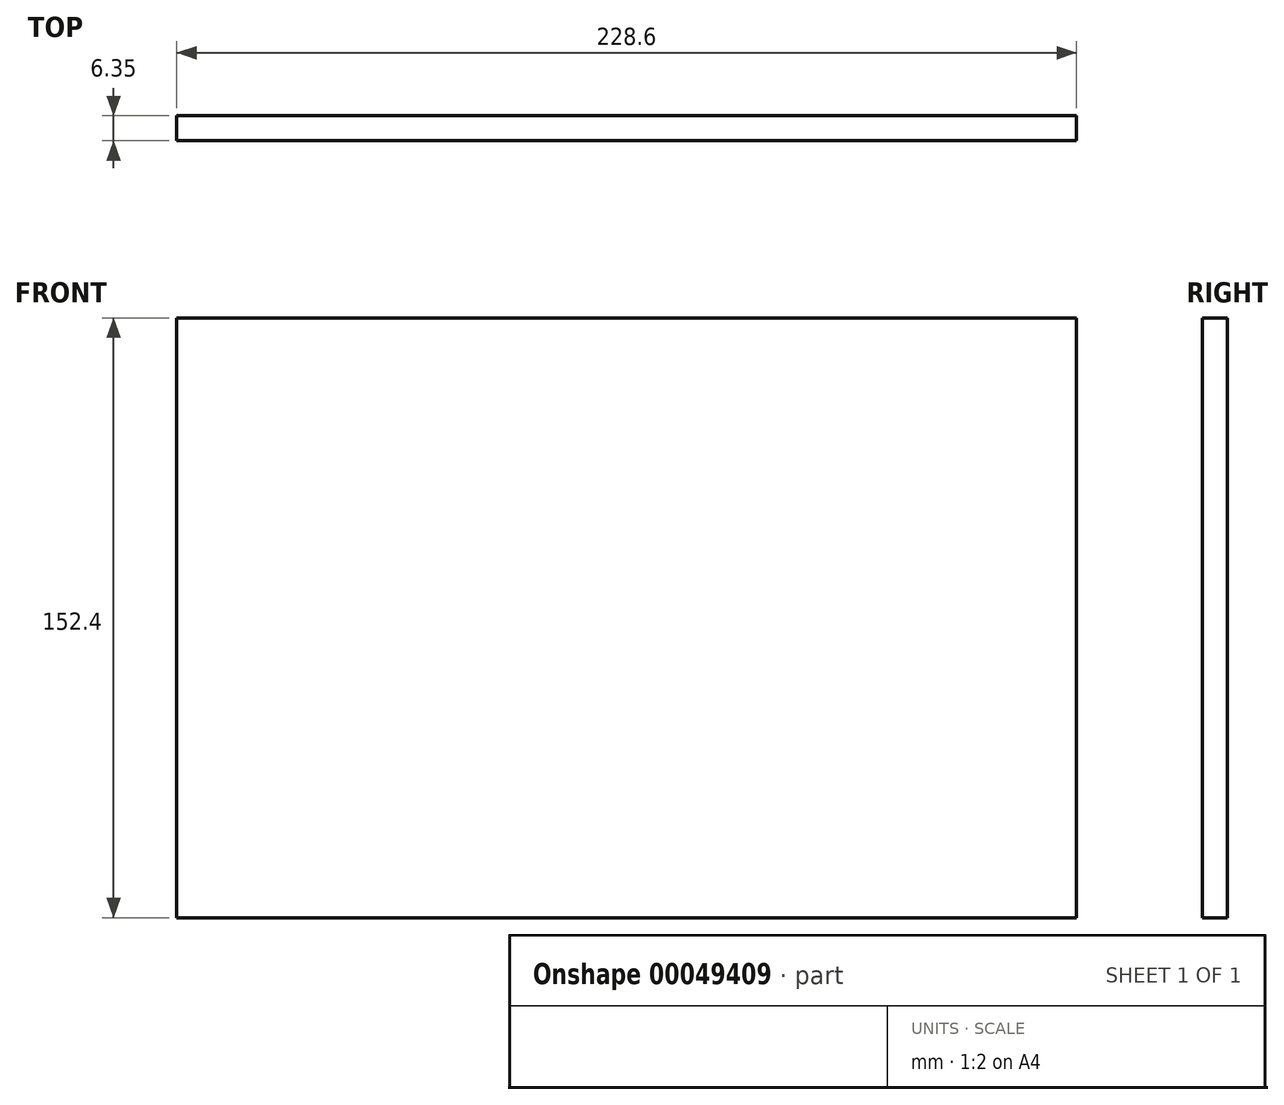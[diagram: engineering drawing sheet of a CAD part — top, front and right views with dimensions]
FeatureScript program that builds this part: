
annotation { "Feature Type Name" : "Feature", "Feature Type Description" : "" }
export const myFeature = defineFeature(function(context is Context, id is Id, definition is map)
    precondition{}
    {
        {
            var Q0;
            Q0=qCreatedBy(makeId("Front.planeOp"),FACE);
            var sketch = newSketch(context, id + "F0", { "sketchPlane" : qUnion([Q0])});
            skLineSegment(sketch, "E0.bottom", {"start": v(-106.81, 114.75) * mm, "end": v(121.79, 114.75) * mm});
            skLineSegment(sketch, "E0.top", {"start": v(-106.81, -37.65) * mm, "end": v(121.79, -37.65) * mm});
            skLineSegment(sketch, "E0.left", {"start": v(-106.81, 114.75) * mm, "end": v(-106.81, -37.65) * mm});
            skLineSegment(sketch, "E0.right", {"start": v(121.79, 114.75) * mm, "end": v(121.79, -37.65) * mm});
            skSolve(sketch);
        }
        {
            var Q0;
            Q0=makeQuery(id+"F0.imprint","IMPRINT",FACE,{"disambiguationData":[TD([[makeQuery(id+"F0.imprint","IMPRINT",EDGE,{"derivedFrom":sQuery(id+"F0.wireOp",EDGE,"E0.bottom")}),-1.0]])]});
            extrude(context, id + "F1", {"entities" : qUnion([Q0]), "depth" : 6.35 * mm});
        }
    });
